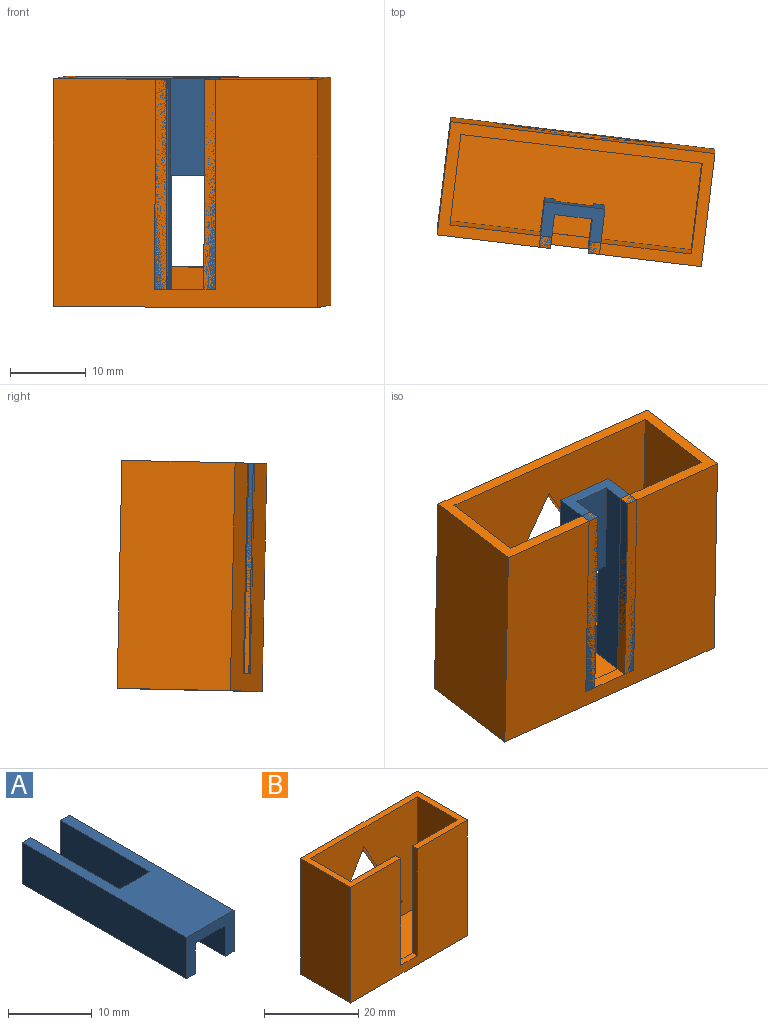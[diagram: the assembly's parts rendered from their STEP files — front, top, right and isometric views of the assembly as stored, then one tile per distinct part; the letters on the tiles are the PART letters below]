
ASSEMBLY  parts=2 mates=1
PART A: 12 faces, bbox 8x27.7x6 mm
  f0: plane 6x1.5mm, normal (0,1,0), area 9mm2, adj f1,f2,f3,f4
  f1: plane 27.73x8mm, normal (0,0,1), area 146.8mm2, adj f0,f2,f4,f6,f8,f9,f10,f11
  f2: plane 27.73x6mm, normal (-1,0,0), area 166.4mm2, adj f0,f1,f3,f9
  f3: plane 27.73x1.5mm, normal (0,0,-1), area 41.6mm2, adj f0,f2,f4,f9
  f4: plane 27.73x6mm, normal (1,0,0), area 147.3mm2, adj f0,f1,f3,f5,f9,f11
  f5: plane 12.73x5mm, normal (0,0,-1), area 63.6mm2, adj f4,f6,f9,f11
  f6: plane 27.73x6mm, normal (-1,0,0), area 147.3mm2, adj f1,f5,f7,f9,f10,f11
  f7: plane 27.73x1.5mm, normal (0,0,-1), area 41.6mm2, adj f6,f8,f9,f10
  f8: plane 27.73x6mm, normal (1,0,0), area 166.4mm2, adj f1,f7,f9,f10
  f9: plane 8x6mm, normal (0,-1,0), area 25.5mm2, adj f1,f2,f3,f4,f5,f6,f7,f8
  f10: plane 6x1.5mm, normal (0,1,0), area 9mm2, adj f1,f6,f7,f8
  f11: plane 5x1.5mm, normal (0,1,0), area 7.5mm2, adj f1,f4,f5,f6
PART B: 17 faces, bbox 35x15x30 mm
  f0: plane 35x15mm, normal (0,0,1), area 133.5mm2, adj f1,f2,f3,f4,f6,f7,f8,f9
  f1: plane 30x15mm, normal (1,0,0), area 450mm2, adj f0,f2,f4,f5
  f2: plane 35x30mm, normal (0,1,0), area 820mm2, adj f0,f1,f3,f5,f14,f15,f16
  f3: plane 30x15mm, normal (-1,0,0), area 450mm2, adj f0,f2,f4,f5
  f4: plane 35x30mm, normal (0,-1,0), area 911.4mm2, adj f0,f1,f3,f5,f11,f12,f13
  f5: plane 35x15mm, normal (0,0,-1), area 525mm2, adj f1,f2,f3,f4
  f6: plane 28.5x12mm, normal (-1,0,0), area 342mm2, adj f0,f7,f9,f10
  f7: plane 32x28.5mm, normal (0,-1,0), area 682mm2, adj f0,f6,f8,f10,f14,f15,f16
  f8: plane 28.5x12mm, normal (1,0,0), area 342mm2, adj f0,f7,f9,f10
  f9: plane 32x28.5mm, normal (0,1,0), area 773.4mm2, adj f0,f6,f8,f10,f11,f12,f13
  f10: plane 32x12mm, normal (0,0,1), area 384mm2, adj f6,f7,f8,f9
  f11: plane 27.73x1.5mm, normal (1,0,0), area 41.6mm2, adj f0,f4,f9,f12
  f12: plane 5x1.5mm, normal (0,0,1), area 7.5mm2, adj f4,f9,f11,f13
  f13: plane 27.73x1.5mm, normal (-1,0,0), area 41.6mm2, adj f0,f4,f9,f12
  f14: plane 20x11.5mm, normal (-0.87,0,-0.5), area 34.6mm2, adj f2,f7,f15,f16
  f15: plane 23x1.5mm, normal (0,0,1), area 34.5mm2, adj f2,f7,f14,f16
  f16: plane 20x11.5mm, normal (0.87,0,-0.5), area 34.6mm2, adj f2,f7,f14,f15
PLACE A rot(axis=(-1,0.06,-0.06),89deg) t=(4.67,-25.03,-29.68)mm
PLACE B rot(axis=(0.17,0.02,-0.98),7deg) t=(5.32,-19.52,-31.84)mm
MATE planar B.f4 <-> A.f7  axis (-0.12,-0.99,-0.02) through (4.46,-27.6,-2)mm
